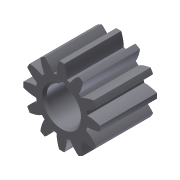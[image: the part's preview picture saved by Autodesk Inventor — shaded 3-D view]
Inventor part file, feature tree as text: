
AUTODESK INVENTOR PART (.ipt)
format: ipt  version: 2011 SP1 (Build 150282100, 282)  size: 213,504 bytes
history: native  units: mm (DEFAULTED — no unit token found)
features: sketch x4, extrude x3, plane x3, other x3, chamfer x1
ambient origin geometry x8: Origin, YZ Plane, XZ Plane, XY Plane, X Axis, Y Axis, Z Axis, Center Point
bodies: Solid1 (feature_tree)
feature tree (14):
  extrude  "Extrusion1"  Depth=13.208mm TaperAngle=0.0deg
  plane  "Work Plane1"
  plane  "Work Plane2"
  plane  "Work Plane3"
  other  "Spur Gear"
  extrude  "Extrusion3"  Depth=76.2mm TaperAngle=0.0deg
  chamfer  "Chamfer1"  Angle=15.0deg  [1 undecoded]
  extrude  "Extrusion4"  Depth=26.67mm TaperAngle=0.0deg
  sketch  "Sketch1"  dims[d0=17.78mm d1=13.208mm d2=0.0mm]
  sketch  "Sketch2"  dims[d3=15.24mm d4=76.2mm d5=0.0mm d6=0.0mm d7=15.0deg]
  other  "Srf1"
  sketch  "Sketch3"  dims[d9=0.0mm d14=0.0mm d15=26.67mm]
  sketch  "Sketch4"  dims[d16=0.0mm d17=0.0mm d18=0.0mm d19=26.67mm d27=8.0mm d28=25.4mm d29=0.0mm d30=0.508mm d31=3.175mm d32=45.0deg d33=2.0mm d34=1.2mm d35=25.4mm d36=0.0mm]
  other  "Pitch Diameter"
note: 1 required parameter value undecoded (feature->parameter linkage not recoverable at this tier; creation-order binding heuristic only, values carry confidence <= 0.55)
